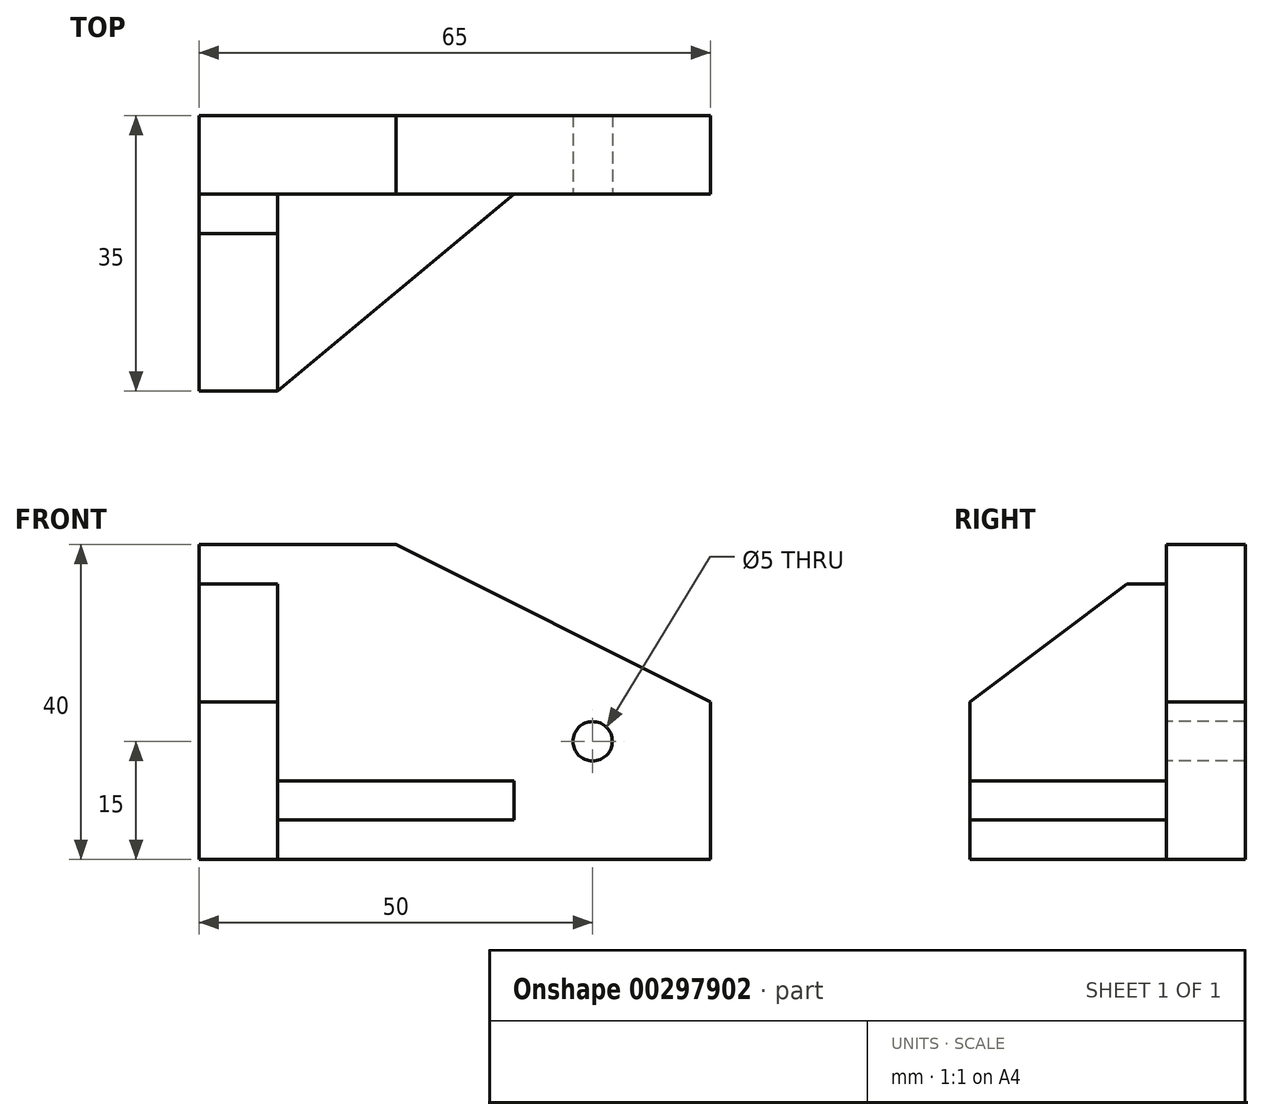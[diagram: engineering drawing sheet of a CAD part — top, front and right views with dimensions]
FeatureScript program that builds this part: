
annotation { "Feature Type Name" : "Feature", "Feature Type Description" : "" }
export const myFeature = defineFeature(function(context is Context, id is Id, definition is map)
    precondition{}
    {
        {
            var Q0;
            Q0=qCreatedBy(makeId("Front.planeOp"),FACE);
            var sketch = newSketch(context, id + "F0", { "sketchPlane" : qUnion([Q0])});
            skLineSegment(sketch, "E0.bottom", {"start": v(-32.5, 20) * mm, "end": v(32.5, 20) * mm});
            skLineSegment(sketch, "E0.top", {"start": v(-32.5, -20) * mm, "end": v(32.5, -20) * mm});
            skLineSegment(sketch, "E0.left", {"start": v(-32.5, 20) * mm, "end": v(-32.5, -20) * mm});
            skLineSegment(sketch, "E0.right", {"start": v(32.5, 20) * mm, "end": v(32.5, -20) * mm});
            skPoint(sketch, "E0.middle", {"position": v(0, 0) * mm});
            skSolve(sketch);
        }
        {
            var Q0;
            Q0 = qSketchRegion(id + "F0", true);
            extrude(context, id + "F1", {"entities" : qUnion([Q0]), "depth" : 35 * mm});
        }
        {
            var Q0;
            Q0=makeQuery(id+"F1.opExtrude","CAP_FACE",FACE,{"disambiguationData":[OSD([sQuery(id+"F0.wireOp",EDGE,"E0.bottom"),sQuery(id+"F0.wireOp",EDGE,"E0.top"),sQuery(id+"F0.wireOp",EDGE,"E0.left"),sQuery(id+"F0.wireOp",EDGE,"E0.right")])],"isStart":false});
            var sketch = newSketch(context, id + "F2", { "sketchPlane" : qUnion([Q0])});
            skLineSegment(sketch, "E1.bottom", {"start": v(-22.5, 20) * mm, "end": v(32.5, 20) * mm});
            skLineSegment(sketch, "E1.top", {"start": v(-22.5, -20) * mm, "end": v(32.5, -20) * mm});
            skLineSegment(sketch, "E1.left", {"start": v(-22.5, 20) * mm, "end": v(-22.5, -20) * mm});
            skLineSegment(sketch, "E1.right", {"start": v(32.5, 20) * mm, "end": v(32.5, -20) * mm});
            skSolve(sketch);
        }
        {
            var Q0;
            Q0 = qSketchRegion(id + "F2", true);
            extrude(context, id + "F3", {"entities" : qUnion([Q0]), "operationType" : NewBodyOperationType.REMOVE, "oppositeDirection" : true, "depth" : 25 * mm});
        }
        {
            var Q0;
            Q0=makeQuery(id+"F1.opExtrude","SWEPT_FACE",FACE,{"disambiguationData":[OSD([sQuery(id+"F0.wireOp",EDGE,"E0.left")])]});
            var sketch = newSketch(context, id + "F4", { "sketchPlane" : qUnion([Q0])});
            skLineSegment(sketch, "E2.bottom", {"start": v(10, 20) * mm, "end": v(15, 20) * mm});
            skLineSegment(sketch, "E2.top", {"start": v(10, 15) * mm, "end": v(15, 15) * mm});
            skLineSegment(sketch, "E2.left", {"start": v(10, 20) * mm, "end": v(10, 15) * mm});
            skLineSegment(sketch, "E2.right", {"start": v(15, 20) * mm, "end": v(15, 15) * mm});
            skSolve(sketch);
        }
        {
            var Q0;
            Q0 = qSketchRegion(id + "F4", true);
            extrude(context, id + "F5", {"entities" : qUnion([Q0]), "operationType" : NewBodyOperationType.REMOVE, "endBound" : BoundingType.THROUGH_ALL, "oppositeDirection" : true, "depth" : 25 * mm});
        }
        {
            var Q0;
            Q0=makeQuery(id+"F5.boolean.opBoolean","MERGE",FACE,{"derivedFrom":[makeQuery(id+"F3.boolean.opBoolean","COPY",FACE,{"derivedFrom":makeQuery(id+"F3.opExtrude","CAP_FACE",FACE,{"disambiguationData":[OSD([sQuery(id+"F2.wireOp",EDGE,"E1.bottom"),sQuery(id+"F2.wireOp",EDGE,"E1.top"),sQuery(id+"F2.wireOp",EDGE,"E1.left"),sQuery(id+"F2.wireOp",EDGE,"E1.right")])],"isStart":false})}),makeQuery(id+"F5.opExtrude","SWEPT_FACE",FACE,{"disambiguationData":[OSD([sQuery(id+"F4.wireOp",EDGE,"E2.left")])]})]});
            var sketch = newSketch(context, id + "F6", { "sketchPlane" : qUnion([Q0])});
            skCircle(sketch, "E3", {"center": v(17.5, -5) * mm, "radius": 2.5 * mm});
            skSolve(sketch);
        }
        {
            var Q0;
            Q0 = qSketchRegion(id + "F6", true);
            extrude(context, id + "F7", {"entities" : qUnion([Q0]), "operationType" : NewBodyOperationType.REMOVE, "endBound" : BoundingType.THROUGH_ALL, "oppositeDirection" : true, "depth" : 25 * mm});
        }
        {
            var Q0;
            Q0=makeQuery(id+"F1.opExtrude","SWEPT_FACE",FACE,{"disambiguationData":[OSD([sQuery(id+"F0.wireOp",EDGE,"E0.left")])]});
            var sketch = newSketch(context, id + "F8", { "sketchPlane" : qUnion([Q0])});
            skLineSegment(sketch, "E4", {"start": v(15, 15) * mm, "end": v(35, 0) * mm});
            skLineSegment(sketch, "E5", {"start": v(35, 0) * mm, "end": v(35, 20) * mm});
            skLineSegment(sketch, "E6", {"start": v(35, 20) * mm, "end": v(15, 20) * mm});
            skLineSegment(sketch, "E7", {"start": v(15, 20) * mm, "end": v(15, 15) * mm});
            skSolve(sketch);
        }
        {
            var Q0;
            Q0 = qSketchRegion(id + "F8", true);
            extrude(context, id + "F9", {"entities" : qUnion([Q0]), "operationType" : NewBodyOperationType.REMOVE, "endBound" : BoundingType.THROUGH_ALL, "oppositeDirection" : true, "depth" : 25 * mm});
        }
        {
            var Q0;
            Q0=makeQuery(id+"F1.opExtrude","CAP_FACE",FACE,{"disambiguationData":[OSD([sQuery(id+"F0.wireOp",EDGE,"E0.bottom"),sQuery(id+"F0.wireOp",EDGE,"E0.top"),sQuery(id+"F0.wireOp",EDGE,"E0.left"),sQuery(id+"F0.wireOp",EDGE,"E0.right")])],"isStart":true});
            var sketch = newSketch(context, id + "F10", { "sketchPlane" : qUnion([Q0])});
            skLineSegment(sketch, "E8", {"start": v(-32.5, 20) * mm, "end": v(7.5, 20) * mm});
            skLineSegment(sketch, "E9", {"start": v(7.5, 20) * mm, "end": v(-32.5, 0) * mm});
            skLineSegment(sketch, "E10", {"start": v(-32.5, 0) * mm, "end": v(-32.5, 20) * mm});
            skSolve(sketch);
        }
        {
            var Q0;
            Q0 = qSketchRegion(id + "F10", true);
            extrude(context, id + "F11", {"entities" : qUnion([Q0]), "operationType" : NewBodyOperationType.REMOVE, "endBound" : BoundingType.THROUGH_ALL, "oppositeDirection" : true, "depth" : 25 * mm});
        }
        {
            var Q0;
            Q0=makeQuery(id+"F5.boolean.opBoolean","MERGE",FACE,{"derivedFrom":[makeQuery(id+"F3.boolean.opBoolean","COPY",FACE,{"derivedFrom":makeQuery(id+"F3.opExtrude","CAP_FACE",FACE,{"disambiguationData":[OSD([sQuery(id+"F2.wireOp",EDGE,"E1.bottom"),sQuery(id+"F2.wireOp",EDGE,"E1.top"),sQuery(id+"F2.wireOp",EDGE,"E1.left"),sQuery(id+"F2.wireOp",EDGE,"E1.right")])],"isStart":false})}),makeQuery(id+"F5.opExtrude","SWEPT_FACE",FACE,{"disambiguationData":[OSD([sQuery(id+"F4.wireOp",EDGE,"E2.left")])]})]});
            var sketch = newSketch(context, id + "F12", { "sketchPlane" : qUnion([Q0])});
            skLineSegment(sketch, "E11", {"start": v(-22.5, -15) * mm, "end": v(9.26, -15) * mm});
            skLineSegment(sketch, "E12", {"start": v(7.5, -15) * mm, "end": v(7.5, -10) * mm});
            skLineSegment(sketch, "E13", {"start": v(7.5, -10) * mm, "end": v(-22.5, -10) * mm});
            skSolve(sketch);
        }
        {
            var Q0;
            {var subQ3=sQuery(id+"F12.wireOp",EDGE,"E12");Q0=makeQuery(id+"F12.imprint","IMPRINT",FACE,{"disambiguationData":[TD([[makeQuery(id+"F12.imprint","IMPRINT",EDGE,{"derivedFrom":subQ3}),1.0]])]});}
            extrude(context, id + "F13", {"entities" : qUnion([Q0]), "operationType" : NewBodyOperationType.ADD, "depth" : 25 * mm});
        }
        {
            var Q0;
            Q0=makeQuery(id+"F13.opExtrude","SWEPT_FACE",FACE,{"disambiguationData":[OSD([sQuery(id+"F12.wireOp",EDGE,"E13")])]});
            var sketch = newSketch(context, id + "F14", { "sketchPlane" : qUnion([Q0])});
            skLineSegment(sketch, "E14", {"start": v(-22.5, -35) * mm, "end": v(7.5, -10) * mm});
            skLineSegment(sketch, "E15", {"start": v(7.5, -10) * mm, "end": v(7.5, -35) * mm});
            skLineSegment(sketch, "E16", {"start": v(7.5, -35) * mm, "end": v(-22.5, -35) * mm});
            skSolve(sketch);
        }
        {
            var Q0;
            Q0 = qSketchRegion(id + "F14", true);
            extrude(context, id + "F15", {"entities" : qUnion([Q0]), "operationType" : NewBodyOperationType.REMOVE, "endBound" : BoundingType.THROUGH_ALL, "oppositeDirection" : true, "depth" : 25 * mm});
        }
    });
